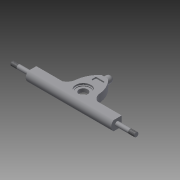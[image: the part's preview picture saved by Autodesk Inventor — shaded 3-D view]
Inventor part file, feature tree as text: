
AUTODESK INVENTOR PART (.ipt)
format: ipt  version: 2015 (Build 190159000, 159)  size: 361,984 bytes
history: native  units: in
note: dims shown in document units (in); Inventor stores cm internally (conversion verified against a paired STEP export)
features: extrude x11, other x7, fillet x5, sketch x4, thread x2, projected_geometry x2, hole x1
ambient origin geometry x8: Origin, YZ Plane, XZ Plane, XY Plane, X Axis, Y Axis, Z Axis, Center Point
bodies: Solid1 (feature_tree)
feature tree (32):
  other  "Axle"
  extrude  "Extrusion11"  Depth=0.78in
  extrude  "Extrusion1"  Depth=0.3125in
  extrude  "Extrusion2"  Depth=3.543in TaperAngle=0.0deg
  extrude  "Extrusion3"  Depth=0.019in
  extrude  "Extrusion4"  Depth=0.019in
  fillet  "Fillet1"  Radius=0.5in
  fillet  "Fillet2"  Radius=0.25in
  extrude  "Extrusion5"  Depth=0.019in
  fillet  "Fillet3"  Radius=0.0in
  fillet  "Fillet4"  Radius=1.9685in
  hole  "Hole"  [1 undecoded]
  extrude  "Extrusion6"  Depth=0.019in
  other  "Outer Hole Depth"
  extrude  "Extrusion7"  TaperAngle=0.0deg  [1 undecoded]
  other  "Outer Hole 2 Depth"
  extrude  "Extrusion8"  Depth=0.019in TaperAngle=0.0deg
  extrude  "Extrusion9"  Depth=0.019in TaperAngle=0.0deg
  extrude  "Extrusion10"  Depth=0.019in
  thread  "Thread1"  [1 undecoded]
  thread  "Thread2"  [1 undecoded]
  fillet  "Fillet5"  Radius=0.32in
  other  "Vertical Axis"
  other  "Axle Axis"
  other  "Work Point1"
  sketch  "Sketch3"  dims[d0=0.71in d1=0.78in]
  projected_geometry  "Projected Loop1"
  sketch  "Sketch4"  dims[d2=2.7559in d4=0.0in d5=0.3125in]
  projected_geometry  "Projected Loop2"
  sketch  "Sketch6"  dims[d6=0.3365in d7=3.543in d8=0.0in d9=9.1252in d10=0.0in]
  sketch  "Sketch7"  dims[d13=1.9in d14=0.0in d17=0.06in d18=0.5in d19=0.5in d20=0.0in d21=0.25in d22=0.7in d23=0.0in d24=0.0in d25=1.9685in d26=0.7874in d27=0.635in d31=0.0in d32=0.0in d33=0.225in d34=0.0in d35=0.17in d36=0.0in d37=0.988in d38=0.655in d39=0.345in d40=0.32in d41=0.05in d42=0.1in d43=0.0in d44=0.622in d45=0.58in d46=0.481in d47=0.35in d48=0.3in d49=0.025in d50=0.0in d51=0.45in d52=0.0in d53=0.45in d54=0.0in d55=0.019in d59=1.75in d62=1.1176in d64=-0.225in d65=-0.17in d66=0.6693in d68=0.0in]
  other  "Kingpin Axis"
note: 4 required parameter values undecoded (feature->parameter linkage not recoverable at this tier; creation-order binding heuristic only, values carry confidence <= 0.55)
